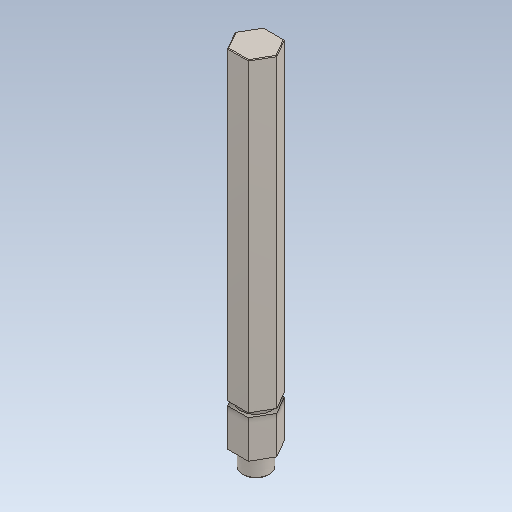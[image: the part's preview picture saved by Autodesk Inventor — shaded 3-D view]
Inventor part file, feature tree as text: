
AUTODESK INVENTOR PART (.ipt)
format: ipt  version: 2020.2 (Build 242310000, 310)  size: 100,864 bytes
history: native  units: in
note: dims shown in document units (in); Inventor stores cm internally (conversion verified against a paired STEP export)
features: chamfer x1
ambient origin geometry x8: Origin, YZ Plane, XZ Plane, XY Plane, X Axis, Y Axis, Z Axis, Center Point
bodies: Solid1 (feature_tree)
feature tree (1):
  chamfer  "Chamfer1"  [1 undecoded]
note: 1 required parameter value undecoded (feature->parameter linkage not recoverable at this tier; creation-order binding heuristic only, values carry confidence <= 0.55)
